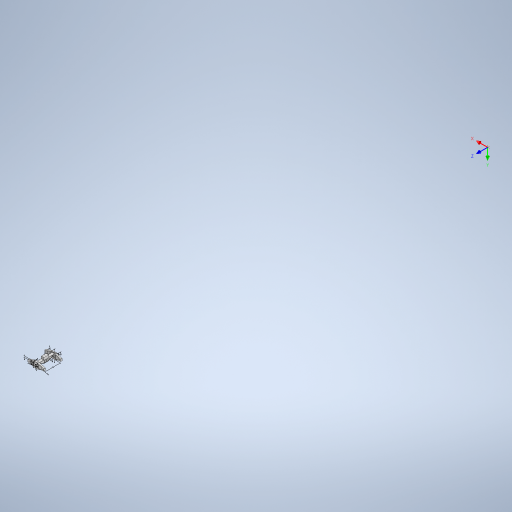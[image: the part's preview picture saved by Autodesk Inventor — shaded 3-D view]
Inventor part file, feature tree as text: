
AUTODESK INVENTOR PART (.ipt)
format: ipt  version: 2023 (Build 270158000, 158)  size: 1,614,848 bytes
history: native  units: in
note: dims shown in document units (in); Inventor stores cm internally (conversion verified against a paired STEP export)
features: other x33, extrude x10, mirror x9, sketch x9, fillet x2, direct_edit x1
ambient origin geometry x8: Origin, YZ Plane, XZ Plane, XY Plane, X Axis, Y Axis, Z Axis, Center Point
bodies: Solid1 (feature_tree), Solid3 (feature_tree)
feature tree (64):
  other  "Annotations"
  extrude  "Extrusion1"  Depth=25.0in
  extrude  "Extrusion2"  Depth=21.574in
  mirror  "Mirror1"
  fillet  "Fillet1"  Radius=37.4168in
  extrude  "Extrusion3"  Depth=10.0in
  mirror  "Mirror2"
  extrude  "Extrusion4"  Depth=12.0312in TaperAngle=0.0deg
  mirror  "Mirror3"
  fillet  "Fillet2"  Radius=1.2in
  other  "UCS1"
  extrude  "Extrusion6"  Depth=1.2in
  extrude  "Extrusion7"  Depth=1.2in
  mirror  "Mirror4"
  extrude  "Extrusion8"  Depth=1.2in
  mirror  "Mirror5"
  mirror  "Mirror6"
  extrude  "Extrusion9"  Depth=1.2in
  extrude  "Extrusion11"  Depth=0.2537in TaperAngle=0.0deg
  mirror  "Mirror7"
  extrude  "Extrusion12"  Depth=0.2537in
  mirror  "Mirror8"
  mirror  "Mirror9"
  direct_edit  "Direct Edit1"
  sketch  "Sketch1"  dims[d0=12.0in d1=25.0in]
  sketch  "Sketch2"  dims[d2=9.625in d3=21.574in d4=37.4168in]
  sketch  "Sketch4"  dims[d5=0.0in d6=10.0in]
  sketch  "Sketch5"  dims[d7=7.2188in d8=12.0312in d9=0.0in d13=1.2in]
  sketch  "Sketch6"  dims[d14=1.2in d15=1.2in]
  sketch  "Sketch8"  dims[d16=7.2188in d17=1.2in]
  sketch  "Sketch9"  dims[d18=1.2in d20=1.2in]
  sketch  "Sketch11"  dims[d24=1.2in d26=1.2in]
  sketch  "Sketch12"  dims[d27=1.2in d28=1.0in d29=0.0in d30=1.2in d43=18.5in d44=18.5in d46=1.0in d47=1.2in d48=1.2in d49=0.5in d50=2.4in d51=0.0in d53=7.15in d54=4.7307in d55=4.7307in d56=0.5in d57=0.5in d59=0.5in d60=1.2in d61=2.4in d62=0.0in d65=0.5in d66=0.0in d67=0.0in d68=0.0in d69=0.0in d70=0.0in d71=0.0in d74=33.0in d75=8.5in d77=10.0in d78=18.0in d80=5.4in d81=6.35in d82=26.0in d85=2.5in d86=8.6in d87=6.0in d88=9.2in d89=0.5in d90=0.5in d91=7.0in d92=0.0in d93=3.0in d94=2.5in d100=1.0in d101=0.0in d103=2.81in d104=11.75in d105=33.0in d106=0.0in d107=0.0in d108=1.0in d109=5.0in d110=0.0in d114=4.9909in d115=0.0in d116=3.0in d117=4.9909in d118=3.0in d119=13.88in d120=0.0in d124=4.64in d125=0.0in d127=4.85in d128=0.0in d129=0.0in d130=0.0in d131=2.3in d139=2.5in d140=2.0in d169=0.0in d182=0.0166in d183=0.3937in d184=0.3937in d187=0.0in d144=0.0456in d145=0.7406in d146=0.0623in d147=0.3802in d148=0.3052in d149=0.1962in d150=0.2486in d152=0.7906in d153=0.211in d154=0.2096in d155=0.1743in d156=0.2959in d157=0.2292in d158=0.1681in d159=0.2529in d160=0.2666in d161=0.1615in d162=0.7406in d163=0.3241in d164=0.0132in d165=0.3052in d166=0.278in d167=0.1528in d168=0.4241in d170=0.1582in d171=0.2564in d172=3.105in d173=0.3168in d174=0.3382in d175=0.2486in d176=0.0in d177=0.3937in d178=0.6849in d179=0.2125in d180=0.2497in d181=0.1057in d185=2.4203in d186=0.1188in d188=0.2122in d189=0.2172in d190=0.2in d191=1.8299in d192=0.211in d193=0.329in d194=0.0595in d195=0.2959in d196=0.1164in d197=0.0143in d198=0.5361in d199=0.0568in d200=0.2397in d201=1.1009in d202=0.3771in d203=1.0316in d207=-0.0821in d208=-0.064in d209=0.2537in d64=0.0in]
  other  "UCS1: YZ Plane"
  other  "UCS1: XZ Plane"
  other  "UCS1: XY Plane"
  other  "UCS1: X Axis"
  other  "UCS1: Y Axis"
  other  "UCS1: Z Axis"
  other  "UCS1: Center Point"
  other  "Scale1"
  other  "Linear Dimension 1"
  other  "Linear Dimension 2"
  other  "Linear Dimension 3"
  other  "Linear Dimension 4"
  other  "Diameter Dimension 1"
  other  "Linear Dimension 5"
  other  "Linear Dimension 6"
  other  "Linear Dimension 7"
  other  "Linear Dimension 8"
  other  "Linear Dimension 9"
  other  "Linear Dimension 10"
  other  "Linear Dimension 11"
  other  "Linear Dimension 12"
  other  "Linear Dimension 13"
  other  "Linear Dimension 14"
  other  "Diameter Dimension 2"
  other  "Linear Dimension 15"
  other  "Diameter Dimension 3"
  other  "Linear Dimension 16"
  other  "Linear Dimension 17"
  other  "Linear Dimension 18"
  other  "Linear Dimension 19"
  other  "Linear Dimension 20"
